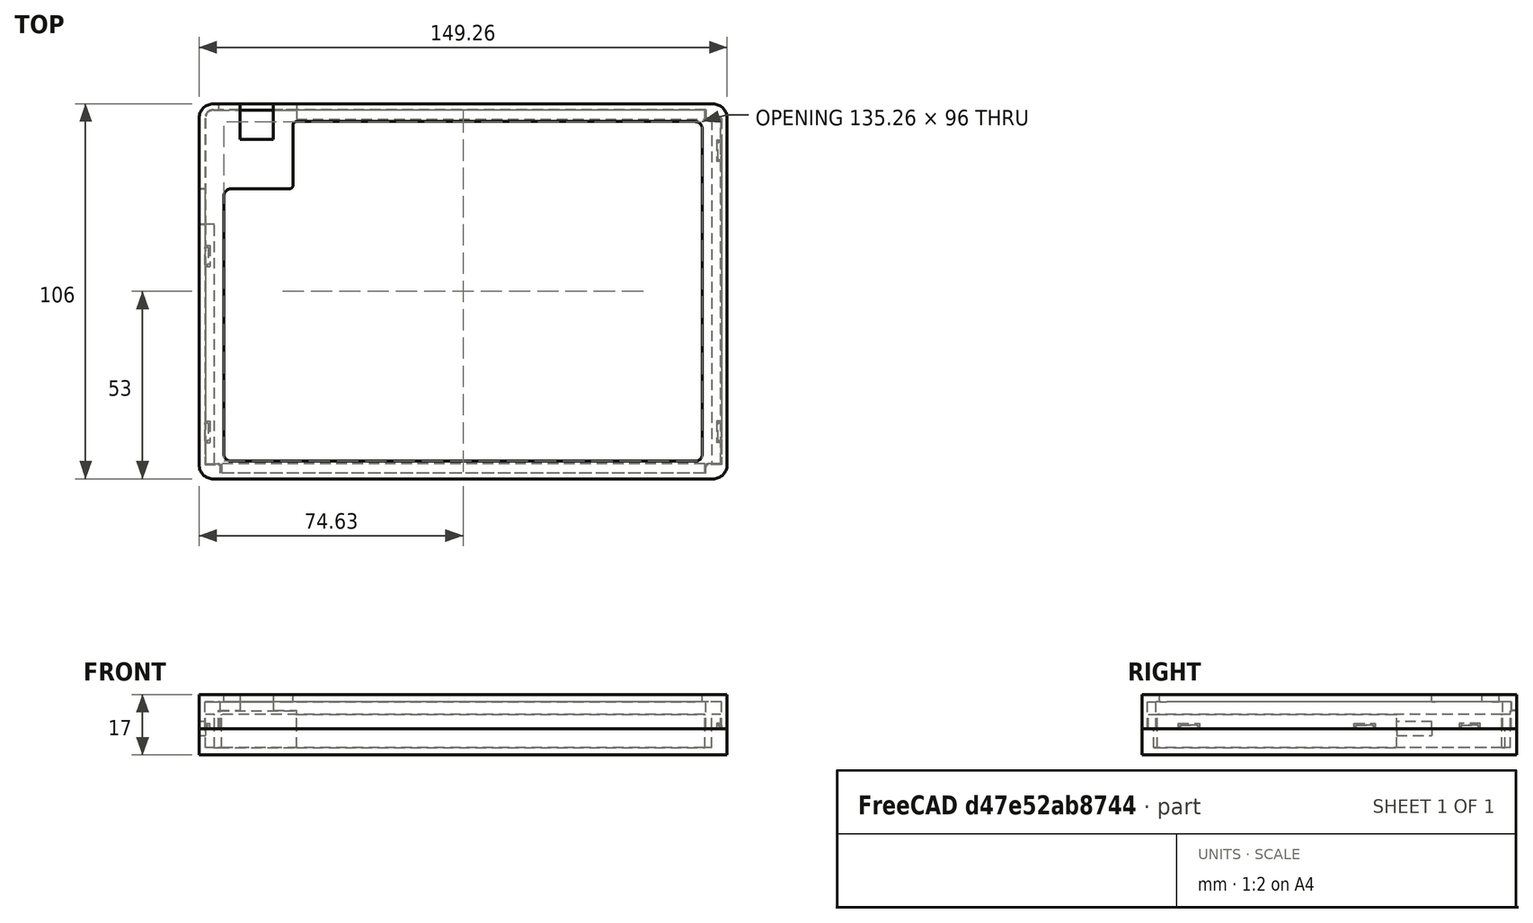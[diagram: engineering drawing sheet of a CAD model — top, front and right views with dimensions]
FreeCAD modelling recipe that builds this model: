
FCSTD DOCUMENT  (FreeCAD 1.0R39109 (Git))
Label: left_v2
License: All rights reserved
LicenseURL: https://en.wikipedia.org/wiki/All_rights_reserved
objects: Sketcher::SketchObject×14, PartDesign::Pad×9, PartDesign::Pocket×5, PartDesign::Body×2, PartDesign::Chamfer×2, Measure::MeasureLength×1, Measure::MeasureDistance×1, App::DocumentObjectGroup×1
note: 78 computed .brp shape members not serialized (recipe doc carries the construction recipe); baked Part::Feature solids carry a one-line shape summary decoded from their .brp

FEATURE [Sketcher::SketchObject] Sketch001
  ArcFitTolerance = 1e-06
  FullyConstrained = true
  MakeInternals = false
  sketch-geometry (8):
    g0: LineSegment StartX=149.26 StartY=102 StartZ=0 EndX=149.26 EndY=4 EndZ=0
    g1: LineSegment StartX=145.26 StartY=3.02e-14 StartZ=0 EndX=4 EndY=0 EndZ=0
    g2: LineSegment StartX=0 StartY=4 StartZ=0 EndX=0 EndY=102 EndZ=0
    g3: LineSegment StartX=4 StartY=106 StartZ=0 EndX=145.26 EndY=106 EndZ=0
    g4: ArcOfCircle CenterX=4 CenterY=102 CenterZ=0 NormalX=0 NormalY=0 NormalZ=1 AngleXU=0 Radius=4 StartAngle=1.5708 EndAngle=3.14159
    g5: ArcOfCircle CenterX=145.26 CenterY=102 CenterZ=0 NormalX=0 NormalY=0 NormalZ=1 AngleXU=0 Radius=4 StartAngle=3e-16 EndAngle=1.5708
    g6: ArcOfCircle CenterX=145.26 CenterY=4 CenterZ=0 NormalX=0 NormalY=0 NormalZ=1 AngleXU=0 Radius=4 StartAngle=4.71239 EndAngle=6.28319
    g7: ArcOfCircle CenterX=4 CenterY=4 CenterZ=0 NormalX=0 NormalY=0 NormalZ=1 AngleXU=0 Radius=4 StartAngle=3.14159 EndAngle=4.71239
  constraints (20):
    c: Vertical(g0)
    c: Vertical(g2)
    c: Horizontal(g3)
    c: Radius(g4) = 4
    c: Tangent(g4,g3) = 1.5708
    c: Tangent(g4,g2) = 1.5708
    c: DistanceX(g3,g3) = 141.26
    c: DistanceX(g1,g1) = 141.26
    c: DistanceY(g2,g2) = 98
    c: DistanceY(g0,g0) = 98
    c: Radius(g5) = 4
    c: Tangent(g5,g3) = 1.5708
    c: Tangent(g5,g0) = 1.5708
    c: Radius(g6) = 4
    c: Tangent(g6,g0) = 1.5708
    c: Tangent(g6,g1) = 1.5708
    c: Tangent(g7,g1) = 1.5708
    c: Tangent(g7,g2) = 1.5708
    c: DistanceX(g2) = 0
    c: DistanceY(g1) = 0
FEATURE [PartDesign::Pad] Pad
  Direction = (0,0,1)
  Length = 2
  Length2 = 10
  Profile = -> Sketch001
  ReferenceAxis = -> Sketch001 [N_Axis]
  Refine = true
  Reversed = true
  Suppressed = false
  Type = 0
FEATURE [Sketcher::SketchObject] Sketch
  ArcFitTolerance = 1e-06
  AttachmentSupport = -> [Pad]
  ExternalGeometry = -> [Pad]
  FullyConstrained = true
  MakeInternals = false
  MapMode = 5
  sketch-geometry (26):
    g0: LineSegment StartX=149.26 StartY=102 StartZ=0 EndX=149.26 EndY=4 EndZ=0
    g1: LineSegment StartX=145.26 StartY=3.02e-14 StartZ=0 EndX=4 EndY=0 EndZ=0
    g2: ArcOfCircle CenterX=145.26 CenterY=102 CenterZ=0 NormalX=0 NormalY=0 NormalZ=1 AngleXU=0 Radius=4 StartAngle=-1.8e-15 EndAngle=1.5708
    g3: ArcOfCircle CenterX=145.26 CenterY=4 CenterZ=0 NormalX=0 NormalY=0 NormalZ=1 AngleXU=0 Radius=4 StartAngle=4.71239 EndAngle=6.28319
    g4: ArcOfCircle CenterX=4 CenterY=4 CenterZ=0 NormalX=0 NormalY=0 NormalZ=1 AngleXU=0 Radius=4 StartAngle=3.14159 EndAngle=4.71239
    g5: ArcOfCircle CenterX=4 CenterY=102 CenterZ=0 NormalX=0 NormalY=0 NormalZ=1 AngleXU=0 Radius=4 StartAngle=1.5708 EndAngle=3.14159
    g6: ArcOfCircle CenterX=4 CenterY=102 CenterZ=0 NormalX=0 NormalY=0 NormalZ=1 AngleXU=0 Radius=2.2 StartAngle=1.5708 EndAngle=3.14159
    g7: LineSegment StartX=1.8 StartY=102 StartZ=0 EndX=1.8 EndY=4.3 EndZ=0
    g8: LineSegment StartX=142.96 StartY=1.8 StartZ=0 EndX=6.3 EndY=1.8 EndZ=0
    g9: LineSegment StartX=5.5 StartY=106 StartZ=0 EndX=5.5 EndY=104.2 EndZ=0
    g10: LineSegment StartX=4 StartY=104.2 StartZ=0 EndX=5.5 EndY=104.2 EndZ=0
    g11: LineSegment StartX=27.5 StartY=106 StartZ=0 EndX=145.26 EndY=106 EndZ=0
    g12: LineSegment StartX=27.5 StartY=106 StartZ=0 EndX=27.5 EndY=104.2 EndZ=0
    g13: LineSegment StartX=27.5 StartY=104.2 StartZ=0 EndX=142.96 EndY=104.2 EndZ=0
    g14: LineSegment StartX=147.46 StartY=101.7 StartZ=0 EndX=147.46 EndY=4.3 EndZ=0
    g15: LineSegment StartX=-2.7e-15 StartY=4 StartZ=0 EndX=-2.7e-15 EndY=102 EndZ=0
    g16: LineSegment StartX=4 StartY=106 StartZ=0 EndX=5.5 EndY=106 EndZ=0
    g17: LineSegment StartX=1.8 StartY=4.3 StartZ=0 EndX=5.3 EndY=4.3 EndZ=0
    g18: LineSegment StartX=6.3 StartY=1.8 StartZ=0 EndX=6.3 EndY=3.3 EndZ=0
    g19: ArcOfCircle CenterX=5.3 CenterY=3.3 CenterZ=0 NormalX=0 NormalY=0 NormalZ=1 AngleXU=0 Radius=1 StartAngle=-9e-16 EndAngle=1.5708
    g20: LineSegment StartX=142.96 StartY=104.2 StartZ=0 EndX=142.96 EndY=102.7 EndZ=0
    g21: LineSegment StartX=147.46 StartY=101.7 StartZ=0 EndX=143.96 EndY=101.7 EndZ=0
    g22: ArcOfCircle CenterX=143.96 CenterY=102.7 CenterZ=0 NormalX=0 NormalY=0 NormalZ=1 AngleXU=0 Radius=1 StartAngle=3.14159 EndAngle=4.71239
    g23: LineSegment StartX=147.46 StartY=4.3 StartZ=0 EndX=143.96 EndY=4.3 EndZ=0
    g24: LineSegment StartX=142.96 StartY=1.8 StartZ=0 EndX=142.96 EndY=3.3 EndZ=0
    g25: ArcOfCircle CenterX=143.96 CenterY=3.3 CenterZ=0 NormalX=0 NormalY=0 NormalZ=1 AngleXU=0 Radius=1 StartAngle=1.5708 EndAngle=3.14159
  constraints (77):
    c: Coincident(g1,g-8)
    c: Coincident(g1,g-10)
    c: Coincident(g2,g-7)
    c: Coincident(g2,g-7)
    c: Coincident(g2,g0)
    c: Coincident(g3,g-8)
    c: Coincident(g3,g1)
    c: Coincident(g4,g1)
    c: Coincident(g5,g-9)
    c: Coincident(g5,g-9)
    c: DistanceX(g5,g9) = 1.5
    c: Angle(g6) = 1.5708
    c: Coincident(g6,g5)
    c: Radius(g6) = 2.2
    c: Coincident(g7,g6)
    c: Vertical(g7)
    c: Horizontal(g8)
    c: Distance(g9) = 1.8
    c: Vertical(g9)
    c: Coincident(g10,g6)
    c: Coincident(g10,g9)
    c: Horizontal(g10)
    c: PointOnObject(g11,g-3)
    c: Coincident(g11,g2)
    c: DistanceX(g9,g11) = 22
    c: Distance(g12) = 1.8
    c: Coincident(g12,g11)
    c: Vertical(g12)
    c: Coincident(g13,g12)
    c: Horizontal(g13)
    c: DistanceX(g14,g0) = 1.8
    c: Tangent(g3,g0) = 1.5708
    c: Angle(g5) = 1.5708
    c: Coincident(g15,g4)
    c: Coincident(g15,g5)
    c: Vertical(g15)
    c: Angle(g4) = 1.5708
    c: Coincident(g16,g5)
    c: Coincident(g16,g9)
    c: Horizontal(g16)
    c: Distance(g17) = 3.5
    c: Horizontal(g17)
    c: DistanceY(g8,g17) = 2.5
    c: Distance(g18) = 1.5
    c: Vertical(g18)
    c: DistanceX(g17,g18) = 4.5
    c: Coincident(g19,g17)
    c: Coincident(g19,g18)
    c: Radius(g19) = 1
    c: Distance(g20) = 1.5
    c: Vertical(g20)
    c: Distance(g21) = 3.5
    c: Horizontal(g21)
    c: DistanceX(g20,g14) = 4.5
    c: DistanceY(g21,g13) = 2.5
    c: Coincident(g22,g20)
    c: Coincident(g22,g21)
    c: Radius(g22) = 1
    c: Distance(g23) = 3.5
    c: Horizontal(g23)
    c: Vertical(g24)
    c: DistanceY(g24,g24) = 1.5
    c: DistanceY(g8,g23) = 2.5
    c: DistanceX(g24,g14) = 4.5
    c: Coincident(g25,g24)
    c: Coincident(g25,g23)
    c: Radius(g25) = 1
    c: Coincident(g14,g21)
    c: Coincident(g13,g20)
    c: Angle(g2) = 1.5708
    c: Coincident(g8,g24)
    c: Coincident(g14,g23)
    c: DistanceX(g14,g0) = 1.8
    c: Coincident(g8,g18)
    c: Coincident(g7,g17)
    c: DistanceY(g1,g8) = 1.8
    c: Radius(g4) = 4
FEATURE [PartDesign::Pad] Pad001
  BaseFeature = -> Pad
  Direction = (0,0,1)
  Length = 5.4
  Length2 = 10
  Profile = -> Sketch
  ReferenceAxis = -> Sketch [N_Axis]
  Refine = true
  Suppressed = false
  Type = 0
FEATURE [Sketcher::SketchObject] Sketch002
  ArcFitTolerance = 1e-06
  AttachmentSupport = -> [Pad001]
  ExternalGeometry = -> [Pad001]
  FullyConstrained = true
  MakeInternals = false
  MapMode = 5
  sketch-geometry (16):
    g0: LineSegment StartX=1.8 StartY=72 StartZ=0 EndX=1.8 EndY=4.3 EndZ=0
    g1: LineSegment StartX=1.8 StartY=4.3 StartZ=0 EndX=4.3 EndY=4.3 EndZ=0
    g2: LineSegment StartX=4.3 StartY=4.3 StartZ=0 EndX=4.3 EndY=72 EndZ=0
    g3: LineSegment StartX=4.3 StartY=72 StartZ=0 EndX=1.8 EndY=72 EndZ=0
    g4: LineSegment StartX=6.3 StartY=1.8 StartZ=0 EndX=142.96 EndY=1.8 EndZ=0
    g5: LineSegment StartX=142.96 StartY=1.8 StartZ=0 EndX=142.96 EndY=4.3 EndZ=0
    g6: LineSegment StartX=142.96 StartY=4.3 StartZ=0 EndX=6.3 EndY=4.3 EndZ=0
    g7: LineSegment StartX=6.3 StartY=4.3 StartZ=0 EndX=6.3 EndY=1.8 EndZ=0
    g8: LineSegment StartX=147.46 StartY=101.7 StartZ=0 EndX=144.96 EndY=101.7 EndZ=0
    g9: LineSegment StartX=144.96 StartY=101.7 StartZ=0 EndX=144.96 EndY=4.3 EndZ=0
    g10: LineSegment StartX=144.96 StartY=4.3 StartZ=0 EndX=147.46 EndY=4.3 EndZ=0
    g11: LineSegment StartX=147.46 StartY=4.3 StartZ=0 EndX=147.46 EndY=101.7 EndZ=0
    g12: LineSegment StartX=142.96 StartY=104.2 StartZ=0 EndX=27.5 EndY=104.2 EndZ=0
    g13: LineSegment StartX=27.5 StartY=104.2 StartZ=0 EndX=27.5 EndY=101.7 EndZ=0
    g14: LineSegment StartX=27.5 StartY=101.7 StartZ=0 EndX=142.96 EndY=101.7 EndZ=0
    g15: LineSegment StartX=142.96 StartY=101.7 StartZ=0 EndX=142.96 EndY=104.2 EndZ=0
  constraints (44):
    c: Coincident(g0,g1)
    c: Coincident(g1,g2)
    c: Coincident(g2,g3)
    c: Coincident(g3,g0)
    c: Vertical(g0)
    c: Vertical(g2)
    c: Horizontal(g1)
    c: Horizontal(g3)
    c: Distance(g0,g2) = 2.5
    c: PointOnObject(g0,g-3)
    c: PointOnObject(g1,g-11)
    c: DistanceY(g0,g-5) = 34
    c: Coincident(g4,g5)
    c: Coincident(g5,g6)
    c: Coincident(g6,g7)
    c: Coincident(g7,g4)
    c: Horizontal(g4)
    c: Horizontal(g6)
    c: Vertical(g5)
    c: Vertical(g7)
    c: Coincident(g4,g-13)
    c: PointOnObject(g5,g-14)
    c: DistanceY(g4,g5) = 2.5
    c: Coincident(g8,g9)
    c: Coincident(g9,g10)
    c: Coincident(g10,g11)
    c: Coincident(g11,g8)
    c: Horizontal(g8)
    c: Horizontal(g10)
    c: Vertical(g9)
    c: Vertical(g11)
    c: Distance(g9,g11) = 2.5
    c: Coincident(g8,g-15)
    c: PointOnObject(g9,g-12)
    c: Coincident(g12,g13)
    c: Coincident(g13,g14)
    c: Coincident(g14,g15)
    c: Coincident(g15,g12)
    c: Horizontal(g14)
    c: Vertical(g13)
    c: Vertical(g15)
    c: Coincident(g12,g-16)
    c: Coincident(g12,g-4)
    c: DistanceY(g13,g12) = 2.5
FEATURE [PartDesign::Pad] Pad002
  BaseFeature = -> Pad001
  Direction = (0,0,1)
  Length = 9.4
  Length2 = 10
  Profile = -> Sketch002
  ReferenceAxis = -> Sketch002 [N_Axis]
  Refine = true
  Suppressed = false
  Type = 0
FEATURE [Sketcher::SketchObject] Sketch003
  ArcFitTolerance = 1e-06
  AttachmentSupport = -> [Pad002]
  ExternalGeometry = -> [Pad002]
  FullyConstrained = true
  MakeInternals = false
  MapMode = 5
  sketch-geometry (4):
    g0: LineSegment StartX=5.5 StartY=106 StartZ=0 EndX=5.5 EndY=104.2 EndZ=0
    g1: LineSegment StartX=5.5 StartY=104.2 StartZ=0 EndX=27.5 EndY=104.2 EndZ=0
    g2: LineSegment StartX=27.5 StartY=104.2 StartZ=0 EndX=27.5 EndY=106 EndZ=0
    g3: LineSegment StartX=27.5 StartY=106 StartZ=0 EndX=5.5 EndY=106 EndZ=0
  constraints (10):
    c: Coincident(g0,g1)
    c: Coincident(g1,g2)
    c: Coincident(g2,g3)
    c: Coincident(g3,g0)
    c: Vertical(g0)
    c: Vertical(g2)
    c: Horizontal(g1)
    c: Horizontal(g3)
    c: Coincident(g0,g-4)
    c: Coincident(g1,g-5)
FEATURE [PartDesign::Pad] Pad003
  BaseFeature = -> Pad002
  Direction = (0,0,1)
  Length = 10.4
  Length2 = 10
  Profile = -> Sketch003
  ReferenceAxis = -> Sketch003 [N_Axis]
  Refine = true
  Suppressed = false
  Type = 0
FEATURE [Sketcher::SketchObject] Sketch004
  ArcFitTolerance = 1e-06
  AttachmentSupport = -> [Pad003]
  ExternalGeometry = -> [Pad003]
  FullyConstrained = true
  MakeInternals = false
  MapMode = 5
  Placement = pos=(0,0,5.4) rot=(0,0,1;0rad)
  sketch-geometry (4):
    g0: LineSegment StartX=-2.7e-15 StartY=82 StartZ=0 EndX=-2.7e-15 EndY=72 EndZ=0
    g1: LineSegment StartX=-2.7e-15 StartY=72 StartZ=0 EndX=1.8 EndY=72 EndZ=0
    g2: LineSegment StartX=1.8 StartY=72 StartZ=0 EndX=1.8 EndY=82 EndZ=0
    g3: LineSegment StartX=1.8 StartY=82 StartZ=0 EndX=-2.7e-15 EndY=82 EndZ=0
  constraints (12):
    c: Coincident(g0,g1)
    c: Coincident(g1,g2)
    c: Coincident(g2,g3)
    c: Coincident(g3,g0)
    c: Vertical(g0)
    c: Vertical(g2)
    c: Horizontal(g1)
    c: Horizontal(g3)
    c: PointOnObject(g0,g-4)
    c: PointOnObject(g1,g-5)
    c: DistanceY(g0,g0) = 10
    c: DistanceY(g0,g-3) = 24
FEATURE [PartDesign::Pocket] Pocket
  BaseFeature = -> Pad003
  Direction = (0,0,-1)
  Length = 2
  Length2 = 5
  Profile = -> Sketch004
  ReferenceAxis = -> Sketch004 [N_Axis]
  Refine = true
  Suppressed = false
  Type = 0
FEATURE [Sketcher::SketchObject] Sketch005
  ArcFitTolerance = 1e-06
  AttachmentSupport = -> [Pocket]
  ExternalGeometry = -> [Pocket]
  FullyConstrained = true
  MakeInternals = false
  MapMode = 5
  Placement = pos=(1.8,0,0) rot=(0.57735,-0.57735,-0.57735;2.0944rad)
  sketch-geometry (8):
    g0: LineSegment StartX=-66 StartY=5.4 StartZ=0 EndX=-60 EndY=5.4 EndZ=0
    g1: LineSegment StartX=-60 StartY=5.4 StartZ=0 EndX=-60 EndY=6.9 EndZ=0
    g2: LineSegment StartX=-60 StartY=6.9 StartZ=0 EndX=-66 EndY=6.9 EndZ=0
    g3: LineSegment StartX=-66 StartY=6.9 StartZ=0 EndX=-66 EndY=5.4 EndZ=0
    g4: LineSegment StartX=-16.3 StartY=5.4 StartZ=0 EndX=-10.3 EndY=5.4 EndZ=0
    g5: LineSegment StartX=-10.3 StartY=5.4 StartZ=0 EndX=-10.3 EndY=6.9 EndZ=0
    g6: LineSegment StartX=-10.3 StartY=6.9 StartZ=0 EndX=-16.3 EndY=6.9 EndZ=0
    g7: LineSegment StartX=-16.3 StartY=6.9 StartZ=0 EndX=-16.3 EndY=5.4 EndZ=0
  constraints (24):
    c: Coincident(g0,g1)
    c: Coincident(g1,g2)
    c: Coincident(g2,g3)
    c: Coincident(g3,g0)
    c: Horizontal(g0)
    c: Horizontal(g2)
    c: Vertical(g1)
    c: Vertical(g3)
    c: Distance(g1,g3) = 6
    c: Distance(g0,g2) = 1.5
    c: PointOnObject(g0,g-4)
    c: Coincident(g4,g5)
    c: Coincident(g5,g6)
    c: Coincident(g6,g7)
    c: Coincident(g7,g4)
    c: Horizontal(g4)
    c: Horizontal(g6)
    c: Vertical(g5)
    c: Vertical(g7)
    c: Distance(g5,g7) = 6
    c: Distance(g4,g6) = 1.5
    c: PointOnObject(g4,g-4)
    c: DistanceX(g-4,g0) = 6
    c: DistanceX(g4,g-5) = 6
FEATURE [Sketcher::SketchObject] Sketch006
  ArcFitTolerance = 1e-06
  AttachmentSupport = -> [Pocket]
  ExternalGeometry = -> [Pocket]
  FullyConstrained = true
  MakeInternals = false
  MapMode = 5
  Placement = pos=(147.46,0,0) rot=(0.57735,0.57735,0.57735;2.0944rad)
  sketch-geometry (8):
    g0: LineSegment StartX=10.3 StartY=5.4 StartZ=0 EndX=16.3 EndY=5.4 EndZ=0
    g1: LineSegment StartX=16.3 StartY=5.4 StartZ=0 EndX=16.3 EndY=6.9 EndZ=0
    g2: LineSegment StartX=16.3 StartY=6.9 StartZ=0 EndX=10.3 EndY=6.9 EndZ=0
    g3: LineSegment StartX=10.3 StartY=6.9 StartZ=0 EndX=10.3 EndY=5.4 EndZ=0
    g4: LineSegment StartX=89.7 StartY=5.4 StartZ=0 EndX=95.7 EndY=5.4 EndZ=0
    g5: LineSegment StartX=95.7 StartY=5.4 StartZ=0 EndX=95.7 EndY=6.9 EndZ=0
    g6: LineSegment StartX=95.7 StartY=6.9 StartZ=0 EndX=89.7 EndY=6.9 EndZ=0
    g7: LineSegment StartX=89.7 StartY=6.9 StartZ=0 EndX=89.7 EndY=5.4 EndZ=0
  constraints (24):
    c: Coincident(g0,g1)
    c: Coincident(g1,g2)
    c: Coincident(g2,g3)
    c: Coincident(g3,g0)
    c: Horizontal(g0)
    c: Horizontal(g2)
    c: Vertical(g1)
    c: Vertical(g3)
    c: Distance(g1,g3) = 6
    c: Distance(g0,g2) = 1.5
    c: PointOnObject(g0,g-3)
    c: Coincident(g4,g5)
    c: Coincident(g5,g6)
    c: Coincident(g6,g7)
    c: Coincident(g7,g4)
    c: Horizontal(g4)
    c: Horizontal(g6)
    c: Vertical(g5)
    c: Vertical(g7)
    c: Distance(g5,g7) = 6
    c: Distance(g4,g6) = 1.5
    c: PointOnObject(g4,g-3)
    c: DistanceX(g4,g-5) = 6
    c: DistanceX(g-4,g0) = 6
FEATURE [PartDesign::Pocket] Pocket001
  BaseFeature = -> Pocket
  Direction = (1,0,0)
  Length = 1.2
  Length2 = 5
  Profile = -> Sketch005
  ReferenceAxis = -> Sketch005 [N_Axis]
  Refine = true
  Suppressed = false
  Type = 0
FEATURE [PartDesign::Pocket] Pocket002
  BaseFeature = -> Pocket001
  Direction = (-1,0,0)
  Length = 1.2
  Length2 = 5
  Profile = -> Sketch006
  ReferenceAxis = -> Sketch006 [N_Axis]
  Refine = true
  Suppressed = false
  Type = 0
FEATURE [PartDesign::Body] Body  label="BottomCase"
  AllowCompound = false
  Group = -> [Sketch001,Pad,Sketch,Pad001,Sketch002,Pad002,Sketch003,Pad003,Sketch004,Pocket,Sketch005,Sketch006,Pocket001,Pocket002]
  Origin = -> Origin
  Tip = -> Pocket002
FEATURE [Measure::MeasureLength] Length  label="Length: 4.00 mm"
  Elements = -> [Body]
  Length = 4
FEATURE [Sketcher::SketchObject] Sketch007
  ArcFitTolerance = 1e-06
  AttachmentOffset = pos=(0,0,5.4) rot=(0,0,1;0rad)
  AttachmentSupport = -> [XY_Plane001]
  FullyConstrained = true
  MakeInternals = false
  MapMode = 5
  Placement = pos=(0,0,5.4) rot=(0,0,1;0rad)
  sketch-geometry (26):
    g0: LineSegment StartX=149.26 StartY=102 StartZ=0 EndX=149.26 EndY=4 EndZ=0
    g1: LineSegment StartX=145.26 StartY=0 StartZ=0 EndX=4 EndY=0 EndZ=0
    g2: ArcOfCircle CenterX=145.26 CenterY=102 CenterZ=0 NormalX=0 NormalY=0 NormalZ=1 AngleXU=0 Radius=4 StartAngle=4.0359e-07 EndAngle=1.5708
    g3: ArcOfCircle CenterX=145.26 CenterY=4 CenterZ=0 NormalX=0 NormalY=0 NormalZ=1 AngleXU=0 Radius=4 StartAngle=4.71239 EndAngle=6.28319
    g4: ArcOfCircle CenterX=4 CenterY=4 CenterZ=0 NormalX=0 NormalY=0 NormalZ=1 AngleXU=0 Radius=4 StartAngle=3.14159 EndAngle=4.71239
    g5: ArcOfCircle CenterX=4 CenterY=102 CenterZ=0 NormalX=0 NormalY=0 NormalZ=1 AngleXU=0 Radius=4 StartAngle=1.5708 EndAngle=3.14159
    g6: ArcOfCircle CenterX=4 CenterY=102 CenterZ=0 NormalX=0 NormalY=0 NormalZ=1 AngleXU=0 Radius=2.4 StartAngle=1.5708 EndAngle=3.14159
    g7: LineSegment StartX=1.6 StartY=102 StartZ=0 EndX=1.6 EndY=4 EndZ=0
    g8: LineSegment StartX=143.26 StartY=1.6 StartZ=0 EndX=6 EndY=1.6 EndZ=0
    g9: LineSegment StartX=5.5 StartY=106 StartZ=0 EndX=5.5 EndY=104.4 EndZ=0
    g10: LineSegment StartX=4 StartY=104.4 StartZ=0 EndX=5.5 EndY=104.4 EndZ=0
    g11: LineSegment StartX=27.5 StartY=106 StartZ=0 EndX=145.26 EndY=106 EndZ=0
    g12: LineSegment StartX=27.5 StartY=106 StartZ=0 EndX=27.5 EndY=104.4 EndZ=0
    g13: LineSegment StartX=27.5 StartY=104.4 StartZ=0 EndX=143.26 EndY=104.4 EndZ=0
    g14: LineSegment StartX=147.66 StartY=102 StartZ=0 EndX=147.66 EndY=4 EndZ=0
    g15: LineSegment StartX=0 StartY=4 StartZ=0 EndX=0 EndY=102 EndZ=0
    g16: LineSegment StartX=4 StartY=106 StartZ=0 EndX=5.5 EndY=106 EndZ=0
    g17: LineSegment StartX=1.6 StartY=4 StartZ=0 EndX=5.3 EndY=4 EndZ=0
    g18: LineSegment StartX=6 StartY=1.6 StartZ=0 EndX=6 EndY=3.3 EndZ=0
    g19: ArcOfCircle CenterX=5.3 CenterY=3.3 CenterZ=0 NormalX=0 NormalY=0 NormalZ=1 AngleXU=0 Radius=0.7 StartAngle=2.371e-13 EndAngle=1.5708
    g20: LineSegment StartX=143.26 StartY=104.4 StartZ=0 EndX=143.26 EndY=102.7 EndZ=0
    g21: LineSegment StartX=147.66 StartY=102 StartZ=0 EndX=143.96 EndY=102 EndZ=0
    g22: ArcOfCircle CenterX=143.96 CenterY=102.7 CenterZ=0 NormalX=0 NormalY=0 NormalZ=1 AngleXU=0 Radius=0.7 StartAngle=3.14159 EndAngle=4.71239
    g23: LineSegment StartX=147.66 StartY=4 StartZ=0 EndX=143.96 EndY=4 EndZ=0
    g24: LineSegment StartX=143.26 StartY=1.6 StartZ=0 EndX=143.26 EndY=3.3 EndZ=0
    g25: ArcOfCircle CenterX=143.96 CenterY=3.3 CenterZ=0 NormalX=0 NormalY=0 NormalZ=1 AngleXU=0 Radius=0.7 StartAngle=1.5708 EndAngle=3.14159
  constraints (84):
    c: Coincident(g2,g0)
    c: Coincident(g3,g1)
    c: Coincident(g4,g1)
    c: DistanceX(g5,g9) = 1.5
    c: Angle(g6) = 1.5708
    c: Coincident(g6,g5)
    c: Radius(g6) = 2.4
    c: Coincident(g7,g6)
    c: Vertical(g7)
    c: Horizontal(g8)
    c: Vertical(g9)
    c: Coincident(g10,g6)
    c: Coincident(g10,g9)
    c: Horizontal(g10)
    c: Coincident(g11,g2)
    c: DistanceX(g9,g11) = 22
    c: Coincident(g12,g11)
    c: Vertical(g12)
    c: Coincident(g13,g12)
    c: Horizontal(g13)
    c: Tangent(g3,g0) = 1.5708
    c: Angle(g5) = 1.5708
    c: Coincident(g15,g4)
    c: Coincident(g15,g5)
    c: Vertical(g15)
    c: Angle(g4) = 1.5708
    c: Coincident(g16,g5)
    c: Coincident(g16,g9)
    c: Horizontal(g16)
    c: Horizontal(g17)
    c: Vertical(g18)
    c: Coincident(g19,g17)
    c: Coincident(g19,g18)
    c: Vertical(g20)
    c: Horizontal(g21)
    c: Coincident(g22,g20)
    c: Coincident(g22,g21)
    c: Horizontal(g23)
    c: Vertical(g24)
    c: Coincident(g25,g24)
    c: Coincident(g25,g23)
    c: Coincident(g14,g21)
    c: Coincident(g13,g20)
    c: Angle(g2) = 1.5708
    c: Coincident(g8,g24)
    c: Coincident(g14,g23)
    c: Coincident(g8,g18)
    c: Coincident(g7,g17)
    c: Radius(g4) = 4
    c: DistanceX(g1,g1) = 141.26
    c: DistanceX(g5,g2) = 141.26
    c: DistanceY(g0,g0) = 98
    c: DistanceY(g4,g5) = 98
    c: DistanceY(g1) = 0
    c: DistanceX(g4) = 0
    c: DistanceX(g4,g17) = 5.3
    c: DistanceY(g1,g18) = 3.3
    c: DistanceX(g23,g0) = 5.3
    c: DistanceY(g1,g24) = 3.3
    c: DistanceY(g20,g2) = 3.3
    c: DistanceX(g21,g0) = 5.3
    c: DistanceY(g9,g9) = 1.6
    c: DistanceX(g4,g7) = 1.6
    c: DistanceY(g1,g8) = 1.6
    c: DistanceY(g1,g8) = 1.6
    c: DistanceX(g14,g0) = 1.6
    c: DistanceX(g14,g0) = 1.6
    c: Vertical(g0)
    c: DistanceY(g13,g2) = 1.6
    c: DistanceY(g12,g11) = 1.6
    c: DistanceY(g5,g5) = 4
    c: DistanceX(g4,g1) = 4
    c: DistanceX(g1,g0) = 4
    c: DistanceY(g1,g2) = 106
    c: DistanceX(g20,g0) = 6
    c: DistanceY(g21,g2) = 4
    c: Radius(g22) = 0.7
    c: Radius(g2) = 4
    c: DistanceX(g24,g0) = 6
    c: DistanceY(g1,g23) = 4
    c: Angle(g25) = 1.5708
    c: Angle(g19) = 1.5708
    c: DistanceX(g4,g18) = 6
    c: DistanceY(g1,g17) = 4
FEATURE [PartDesign::Pad] Pad004
  Direction = (0,0,1)
  Length = 7.6
  Length2 = 10
  Profile = -> Sketch007
  ReferenceAxis = -> Sketch007 [N_Axis]
  Refine = true
  Suppressed = false
  Type = 0
FEATURE [Sketcher::SketchObject] Sketch008
  ArcFitTolerance = 1e-06
  AttachmentSupport = -> [Pad004]
  ExternalGeometry = -> [Pad004]
  FullyConstrained = true
  MakeInternals = false
  MapMode = 5
  Placement = pos=(0,0,13) rot=(0,0,1;0rad)
  sketch-geometry (20):
    g0: LineSegment StartX=-1.226e-13 StartY=4 StartZ=0 EndX=0 EndY=102 EndZ=0
    g1: ArcOfCircle CenterX=145.26 CenterY=102 CenterZ=0 NormalX=0 NormalY=0 NormalZ=1 AngleXU=0 Radius=4 StartAngle=-9e-16 EndAngle=1.5708
    g2: ArcOfCircle CenterX=4 CenterY=102 CenterZ=0 NormalX=0 NormalY=0 NormalZ=1 AngleXU=0 Radius=4 StartAngle=1.5708 EndAngle=3.14159
    g3: ArcOfCircle CenterX=4 CenterY=4 CenterZ=0 NormalX=0 NormalY=0 NormalZ=1 AngleXU=0 Radius=4 StartAngle=3.14159 EndAngle=4.71239
    g4: ArcOfCircle CenterX=145.26 CenterY=4 CenterZ=0 NormalX=0 NormalY=0 NormalZ=1 AngleXU=0 Radius=4 StartAngle=4.71239 EndAngle=6.28319
    g5: LineSegment StartX=142.26 StartY=99 StartZ=0 EndX=142.26 EndY=7 EndZ=0
    g6: LineSegment StartX=7 StartY=80 StartZ=0 EndX=7 EndY=7 EndZ=0
    g7: LineSegment StartX=27.5 StartY=101 StartZ=0 EndX=140.26 EndY=101 EndZ=0
    g8: ArcOfCircle CenterX=140.26 CenterY=99 CenterZ=0 NormalX=0 NormalY=0 NormalZ=1 AngleXU=0 Radius=2 StartAngle=1.8e-15 EndAngle=1.5708
    g9: LineSegment StartX=140.26 StartY=5 StartZ=0 EndX=9 EndY=5 EndZ=0
    g10: ArcOfCircle CenterX=140.26 CenterY=7 CenterZ=0 NormalX=0 NormalY=0 NormalZ=1 AngleXU=0 Radius=2 StartAngle=4.71239 EndAngle=6.28319
    g11: ArcOfCircle CenterX=9 CenterY=7 CenterZ=0 NormalX=0 NormalY=0 NormalZ=1 AngleXU=0 Radius=2 StartAngle=3.14159 EndAngle=4.71239
    g12: LineSegment StartX=26.5 StartY=100 StartZ=0 EndX=26.5 EndY=83 EndZ=0
    g13: ArcOfCircle CenterX=27.5 CenterY=100 CenterZ=0 NormalX=0 NormalY=0 NormalZ=1 AngleXU=0 Radius=1 StartAngle=1.5708 EndAngle=3.14159
    g14: LineSegment StartX=9 StartY=82 StartZ=0 EndX=25.5 EndY=82 EndZ=0
    g15: ArcOfCircle CenterX=25.5 CenterY=83 CenterZ=0 NormalX=0 NormalY=0 NormalZ=1 AngleXU=0 Radius=1 StartAngle=4.71239 EndAngle=6.28319
    g16: ArcOfCircle CenterX=9 CenterY=80 CenterZ=0 NormalX=0 NormalY=0 NormalZ=1 AngleXU=0 Radius=2 StartAngle=1.5708 EndAngle=3.14159
    g17: LineSegment StartX=149.26 StartY=4 StartZ=0 EndX=149.26 EndY=102 EndZ=0
    g18: LineSegment StartX=4 StartY=9.1e-14 StartZ=0 EndX=145.26 EndY=0 EndZ=0
    g19: LineSegment StartX=4 StartY=106 StartZ=0 EndX=145.26 EndY=106 EndZ=0
  constraints (63):
    c: Coincident(g0,g-9)
    c: Coincident(g2,g-9)
    c: Coincident(g2,g0)
    c: Coincident(g3,g-8)
    c: Coincident(g1,g-11) = 1.5708
    c: Angle(g1) = 1.5708
    c: Angle(g4) = 1.5708
    c: Tangent(g3,g0) = 1.5708
    c: Angle(g2) = 1.5708
    c: Radius(g1) = 4
    c: Radius(g4) = 4
    c: Vertical(g5)
    c: DistanceX(g5,g4) = 7
    c: Vertical(g6)
    c: DistanceX(g0,g6) = 7
    c: DistanceY(g-7,g5) = 7
    c: Horizontal(g7)
    c: DistanceY(g7,g-11) = 5
    c: DistanceX(g7,g1) = 9
    c: DistanceY(g5,g-11) = 7
    c: Coincident(g8,g7)
    c: Coincident(g8,g5)
    c: Radius(g8) = 2
    c: Horizontal(g9)
    c: DistanceY(g-7,g9) = 5
    c: DistanceX(g9,g4) = 9
    c: Coincident(g10,g5)
    c: Coincident(g10,g9)
    c: Radius(g10) = 2
    c: DistanceX(g0,g9) = 9
    c: DistanceY(g-8,g6) = 7
    c: Coincident(g11,g6)
    c: Coincident(g11,g9)
    c: Radius(g11) = 2
    c: DistanceX(g0,g7) = 27.5
    c: Vertical(g12)
    c: DistanceX(g0,g12) = 26.5
    c: DistanceY(g12,g2) = 6
    c: Coincident(g13,g12)
    c: Coincident(g13,g7)
    c: Horizontal(g14)
    c: DistanceY(g14,g2) = 24
    c: DistanceX(g0,g14) = 25.5
    c: DistanceY(g12,g2) = 23
    c: Coincident(g15,g12)
    c: Coincident(g15,g14)
    c: Radius(g15) = 1
    c: DistanceY(g6,g2) = 26
    c: DistanceX(g0,g14) = 9
    c: Coincident(g16,g6)
    c: Coincident(g16,g14)
    c: Radius(g16) = 2
    c: Radius(g13) = 1
    c: Tangent(g17,g4) = -1.5708
    c: Coincident(g17,g1)
    c: DistanceY(g5,g1) = 3
    c: DistanceY(g4,g4) = 4
    c: DistanceY(g4,g9) = 5
    c: Angle(g3) = 1.5708
    c: Tangent(g18,g3) = -1.5708
    c: Coincident(g18,g4)
    c: Coincident(g19,g2)
    c: Coincident(g19,g1)
FEATURE [PartDesign::Pad] Pad005
  BaseFeature = -> Pad004
  Direction = (0,0,1)
  Length = 2
  Length2 = 10
  Profile = -> Sketch008
  ReferenceAxis = -> Sketch008 [N_Axis]
  Refine = true
  Suppressed = false
  Type = 0
FEATURE [Sketcher::SketchObject] Sketch009
  ArcFitTolerance = 1e-06
  AttachmentSupport = -> [Pad005]
  ExternalGeometry = -> [Pad005]
  FullyConstrained = true
  MakeInternals = false
  MapMode = 5
  Placement = pos=(0,0,15) rot=(0,0,1;0rad)
  sketch-geometry (4):
    g0: LineSegment StartX=11.5 StartY=106 StartZ=0 EndX=11.5 EndY=96 EndZ=0
    g1: LineSegment StartX=11.5 StartY=96 StartZ=0 EndX=21 EndY=96 EndZ=0
    g2: LineSegment StartX=21 StartY=96 StartZ=0 EndX=21 EndY=106 EndZ=0
    g3: LineSegment StartX=21 StartY=106 StartZ=0 EndX=11.5 EndY=106 EndZ=0
  constraints (12):
    c: Coincident(g0,g1)
    c: Coincident(g1,g2)
    c: Coincident(g2,g3)
    c: Coincident(g3,g0)
    c: Vertical(g0)
    c: Vertical(g2)
    c: Horizontal(g1)
    c: Horizontal(g3)
    c: PointOnObject(g0,g-3)
    c: DistanceX(g-4,g0) = 11.5
    c: DistanceX(g0,g2) = 9.5
    c: DistanceY(g0,g0) = 10
FEATURE [PartDesign::Pocket] Pocket003
  BaseFeature = -> Pad005
  Direction = (0,0,-1)
  Length = 2
  Length2 = 5
  Profile = -> Sketch009
  ReferenceAxis = -> Sketch009 [N_Axis]
  Refine = true
  Suppressed = false
  Type = 0
FEATURE [Sketcher::SketchObject] Sketch010
  ArcFitTolerance = 1e-06
  AttachmentSupport = -> [Pocket003]
  ExternalGeometry = -> [Pocket003]
  FullyConstrained = true
  MakeInternals = false
  MapMode = 5
  Placement = pos=(0,0,5.4) rot=(1,0,0;3.14159rad)
  sketch-geometry (4):
    g0: LineSegment StartX=0 StartY=-72 StartZ=0 EndX=0 EndY=-82 EndZ=0
    g1: LineSegment StartX=0 StartY=-82 StartZ=0 EndX=1.6 EndY=-82 EndZ=0
    g2: LineSegment StartX=1.6 StartY=-82 StartZ=0 EndX=1.6 EndY=-72 EndZ=0
    g3: LineSegment StartX=1.6 StartY=-72 StartZ=0 EndX=0 EndY=-72 EndZ=0
  constraints (12):
    c: Coincident(g0,g1)
    c: Coincident(g1,g2)
    c: Coincident(g2,g3)
    c: Coincident(g3,g0)
    c: Vertical(g0)
    c: Vertical(g2)
    c: Horizontal(g1)
    c: Horizontal(g3)
    c: PointOnObject(g1,g-5)
    c: DistanceY(g-3,g1) = 24
    c: DistanceY(g1,g2) = 10
    c: PointOnObject(g0,g-4)
FEATURE [PartDesign::Pocket] Pocket004
  BaseFeature = -> Pocket003
  Direction = (0,0,1)
  Length = 2
  Length2 = 5
  Profile = -> Sketch010
  ReferenceAxis = -> Sketch010 [N_Axis]
  Refine = true
  Suppressed = false
  Type = 0
FEATURE [Sketcher::SketchObject] Sketch011
  ArcFitTolerance = 1e-06
  AttachmentOffset = pos=(0,0,-1.6) rot=(0,0,1;0rad)
  AttachmentSupport = -> [Pocket004]
  ExternalGeometry = -> [Pocket004]
  FullyConstrained = true
  MakeInternals = false
  MapMode = 5
  Placement = pos=(147.66,0,0) rot=(0.57735,0.57735,0.57735;2.0944rad)
  sketch-geometry (8):
    g0: LineSegment StartX=90.2 StartY=5.4 StartZ=0 EndX=95.2 EndY=5.4 EndZ=0
    g1: LineSegment StartX=95.2 StartY=5.4 StartZ=0 EndX=95.2 EndY=6.4 EndZ=0
    g2: LineSegment StartX=95.2 StartY=6.4 StartZ=0 EndX=90.2 EndY=6.4 EndZ=0
    g3: LineSegment StartX=90.2 StartY=6.4 StartZ=0 EndX=90.2 EndY=5.4 EndZ=0
    g4: LineSegment StartX=10.8 StartY=5.4 StartZ=0 EndX=15.8 EndY=5.4 EndZ=0
    g5: LineSegment StartX=15.8 StartY=5.4 StartZ=0 EndX=15.8 EndY=6.4 EndZ=0
    g6: LineSegment StartX=15.8 StartY=6.4 StartZ=0 EndX=10.8 EndY=6.4 EndZ=0
    g7: LineSegment StartX=10.8 StartY=6.4 StartZ=0 EndX=10.8 EndY=5.4 EndZ=0
  constraints (24):
    c: Coincident(g0,g1)
    c: Coincident(g1,g2)
    c: Coincident(g2,g3)
    c: Coincident(g3,g0)
    c: Horizontal(g0)
    c: Horizontal(g2)
    c: Vertical(g1)
    c: Vertical(g3)
    c: Distance(g1,g3) = 5
    c: Distance(g0,g2) = 1
    c: PointOnObject(g0,g-4)
    c: DistanceX(g0,g-5) = 10.8
    c: Coincident(g4,g5)
    c: Coincident(g5,g6)
    c: Coincident(g6,g7)
    c: Coincident(g7,g4)
    c: Horizontal(g4)
    c: Horizontal(g6)
    c: Vertical(g5)
    c: Vertical(g7)
    c: Distance(g5,g7) = 5
    c: Distance(g4,g6) = 1
    c: PointOnObject(g4,g-4)
    c: DistanceX(g-3,g4) = 10.8
FEATURE [PartDesign::Pad] Pad006
  BaseFeature = -> Pocket004
  Direction = (1,0,0)
  Length = 1
  Length2 = 10
  Profile = -> Sketch011
  ReferenceAxis = -> Sketch011 [N_Axis]
  Refine = true
  Reversed = true
  Suppressed = false
  Type = 0
FEATURE [PartDesign::Chamfer] Chamfer
  Angle = 45
  Base = -> Pad006 [Edge170,Edge169]
  BaseFeature = -> Pad006
  ChamferType = 0
  FlipDirection = false
  Refine = true
  Size = 0.99
  Size2 = 1
  SupportTransform = false
  Suppressed = false
  UseAllEdges = false
FEATURE [Sketcher::SketchObject] Sketch012
  ArcFitTolerance = 1e-06
  AttachmentOffset = pos=(0,0,-1.6) rot=(0,0,1;0rad)
  AttachmentSupport = -> [Chamfer]
  ExternalGeometry = -> [Chamfer]
  FullyConstrained = true
  MakeInternals = false
  MapMode = 5
  Placement = pos=(1.6,0,9.9e-15) rot=(0.57735,-0.57735,-0.57735;2.0944rad)
  sketch-geometry (8):
    g0: LineSegment StartX=-10.8 StartY=5.4 StartZ=0 EndX=-10.8 EndY=6.4 EndZ=0
    g1: LineSegment StartX=-10.8 StartY=6.4 StartZ=0 EndX=-15.8 EndY=6.4 EndZ=0
    g2: LineSegment StartX=-15.8 StartY=6.4 StartZ=0 EndX=-15.8 EndY=5.4 EndZ=0
    g3: LineSegment StartX=-15.8 StartY=5.4 StartZ=0 EndX=-10.8 EndY=5.4 EndZ=0
    g4: LineSegment StartX=-65.5 StartY=5.4 StartZ=0 EndX=-60.5 EndY=5.4 EndZ=0
    g5: LineSegment StartX=-60.5 StartY=5.4 StartZ=0 EndX=-60.5 EndY=6.4 EndZ=0
    g6: LineSegment StartX=-60.5 StartY=6.4 StartZ=0 EndX=-65.5 EndY=6.4 EndZ=0
    g7: LineSegment StartX=-65.5 StartY=6.4 StartZ=0 EndX=-65.5 EndY=5.4 EndZ=0
  constraints (24):
    c: Coincident(g0,g1)
    c: Coincident(g1,g2)
    c: Coincident(g2,g3)
    c: Coincident(g3,g0)
    c: Vertical(g0)
    c: Vertical(g2)
    c: Horizontal(g1)
    c: Horizontal(g3)
    c: Distance(g0,g2) = 5
    c: Distance(g1,g3) = 1
    c: PointOnObject(g0,g-4)
    c: Coincident(g4,g5)
    c: Coincident(g5,g6)
    c: Coincident(g6,g7)
    c: Coincident(g7,g4)
    c: Horizontal(g4)
    c: Horizontal(g6)
    c: Vertical(g5)
    c: Vertical(g7)
    c: Distance(g5,g7) = 5
    c: Distance(g4,g6) = 1
    c: PointOnObject(g4,g-4)
    c: DistanceX(g0,g-3) = 10.8
    c: DistanceX(g-5,g4) = 6.5
FEATURE [PartDesign::Pad] Pad007
  BaseFeature = -> Chamfer
  Direction = (-1,0,-6.2e-15)
  Length = 1
  Length2 = 10
  Profile = -> Sketch012
  ReferenceAxis = -> Sketch012 [N_Axis]
  Refine = true
  Reversed = true
  Suppressed = false
  Type = 0
FEATURE [PartDesign::Chamfer] Chamfer001
  Angle = 45
  Base = -> Pad007 [Edge157,Edge156]
  BaseFeature = -> Pad007
  ChamferType = 0
  FlipDirection = false
  Refine = true
  Size = 0.99
  Size2 = 1
  SupportTransform = false
  Suppressed = false
  UseAllEdges = false
FEATURE [Sketcher::SketchObject] Sketch013
  ArcFitTolerance = 1e-06
  AttachmentSupport = -> [Chamfer001]
  ExternalGeometry = -> [Chamfer001]
  FullyConstrained = true
  MakeInternals = false
  MapMode = 5
  Placement = pos=(0,0,13) rot=(1,0,0;3.14159rad)
  sketch-geometry (8):
    g0: LineSegment StartX=5.5 StartY=-104.4 StartZ=0 EndX=5.5 EndY=-106 EndZ=0
    g1: LineSegment StartX=5.5 StartY=-106 StartZ=0 EndX=11.5 EndY=-106 EndZ=0
    g2: LineSegment StartX=11.5 StartY=-106 StartZ=0 EndX=11.5 EndY=-104.4 EndZ=0
    g3: LineSegment StartX=11.5 StartY=-104.4 StartZ=0 EndX=5.5 EndY=-104.4 EndZ=0
    g4: LineSegment StartX=21 StartY=-106 StartZ=0 EndX=27.5 EndY=-106 EndZ=0
    g5: LineSegment StartX=27.5 StartY=-106 StartZ=0 EndX=27.5 EndY=-104.4 EndZ=0
    g6: LineSegment StartX=27.5 StartY=-104.4 StartZ=0 EndX=21 EndY=-104.4 EndZ=0
    g7: LineSegment StartX=21 StartY=-104.4 StartZ=0 EndX=21 EndY=-106 EndZ=0
  constraints (20):
    c: Coincident(g0,g1)
    c: Coincident(g1,g2)
    c: Coincident(g2,g3)
    c: Coincident(g3,g0)
    c: Vertical(g0)
    c: Vertical(g2)
    c: Horizontal(g1)
    c: Horizontal(g3)
    c: Coincident(g0,g-6)
    c: Coincident(g1,g-3)
    c: Coincident(g4,g5)
    c: Coincident(g5,g6)
    c: Coincident(g6,g7)
    c: Coincident(g7,g4)
    c: Horizontal(g4)
    c: Horizontal(g6)
    c: Vertical(g5)
    c: Vertical(g7)
    c: Coincident(g4,g-4)
    c: Coincident(g5,g-5)
FEATURE [PartDesign::Pad] Pad008
  BaseFeature = -> Chamfer001
  Direction = (0,0,-1)
  Length = 2.4
  Length2 = 10
  Profile = -> Sketch013
  ReferenceAxis = -> Sketch013 [N_Axis]
  Refine = true
  Suppressed = false
  Type = 0
FEATURE [PartDesign::Body] Body001  label="TopCover"
  AllowCompound = false
  Group = -> [Sketch007,Pad004,Sketch008,Pad005,Sketch009,Pocket003,Sketch010,Pocket004,Sketch011,Pad006,Chamfer,Sketch012,Pad007,Chamfer001,Sketch013,Pad008]
  Origin = -> Origin001
  Tip = -> Pad008
FEATURE [Measure::MeasureDistance] Distance  label="Distance: 2.60 mm"
  Distance = 2.6
  DistanceX = 1.30718e-06
  DistanceY = 1.30718e-06
  DistanceZ = 2.6
  Element1 = -> Body001 [Chamfer001.Edge141]
  Element2 = -> Body [Pocket002.Edge82]
  Position1 = (5.5,106,13)
  Position2 = (5.5,106,10.4)
FEATURE [App::DocumentObjectGroup] Measurements
  Group = -> [Length,Distance]
